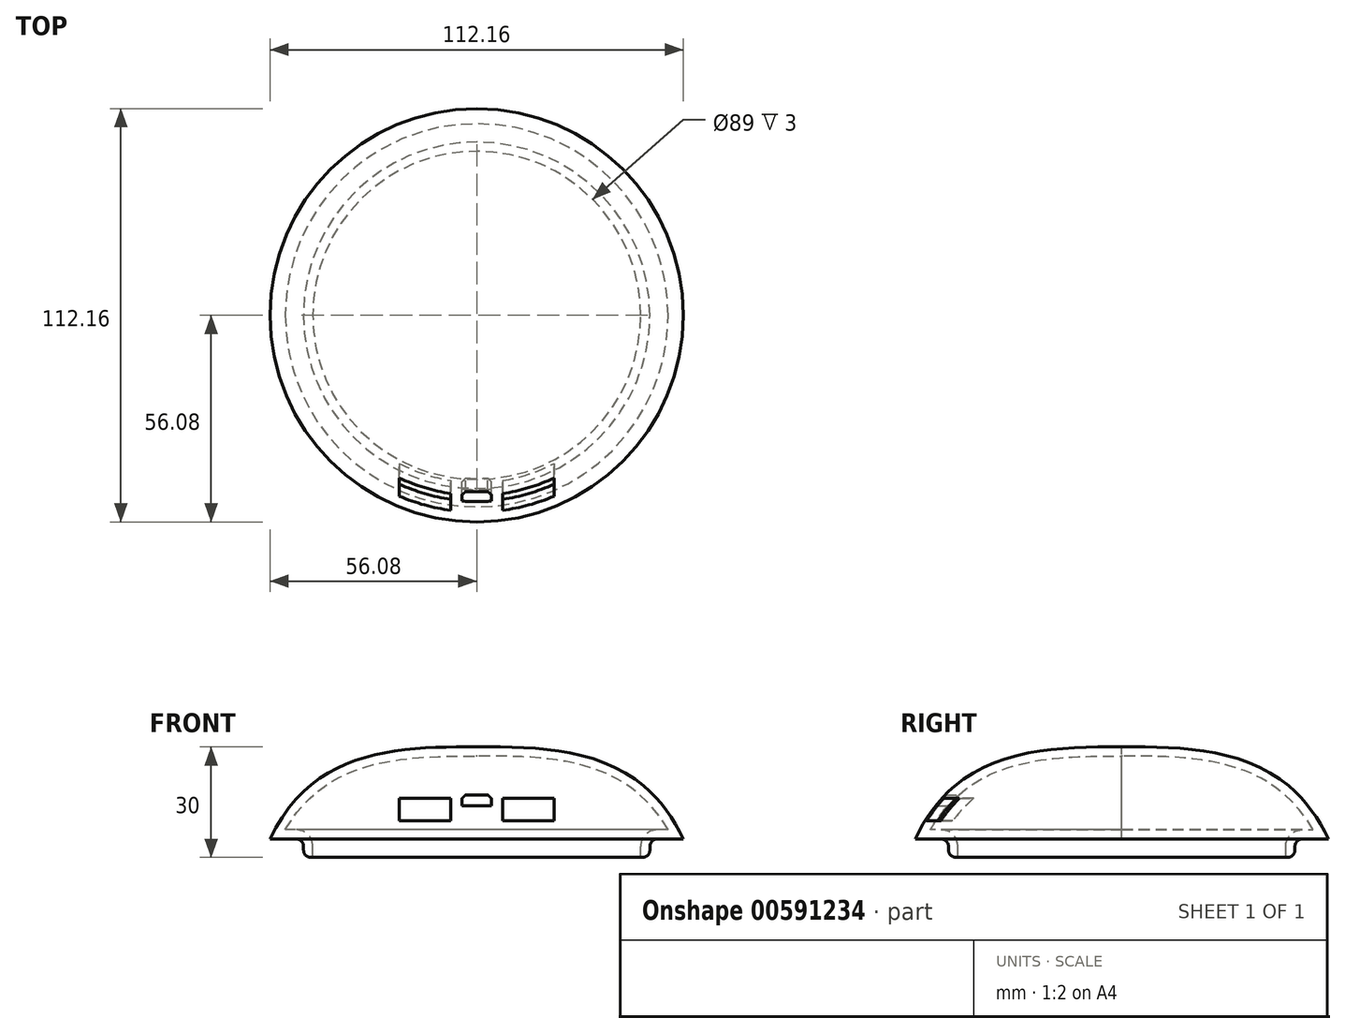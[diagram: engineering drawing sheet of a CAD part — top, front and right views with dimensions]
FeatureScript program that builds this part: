
annotation { "Feature Type Name" : "Feature", "Feature Type Description" : "" }
export const myFeature = defineFeature(function(context is Context, id is Id, definition is map)
    precondition{}
    {
        {
            var Q0;
            Q0=qCreatedBy(makeId("Front.planeOp"),FACE);
            var sketch = newSketch(context, id + "F0", { "sketchPlane" : qUnion([Q0])});
            skLineSegment(sketch, "E0", {"start": v(0, 0) * mm, "end": v(0, 35) * mm, "construction": true});
            skLineSegment(sketch, "E1", {"start": v(0, 0) * mm, "end": v(-45, 0) * mm, "construction": true});
            skFitSpline(sketch, "E2", {"points": [v(0, 35) * mm, v(-48.2, 26.6) * mm, v(-65, 0) * mm], "startDerivative": vector(-121.59, 0) * mm, "endDerivative": vector(-32.6, -91.94) * mm, "construction": true});
            skLineSegment(sketch, "E3", {"start": v(0, 0) * mm, "end": v(-45, 0) * mm});
            skLineSegment(sketch, "E4", {"start": v(-47, 2) * mm, "end": v(-47, 3) * mm});
            skLineSegment(sketch, "E5", {"start": v(-49, 5) * mm, "end": v(-63.16, 5) * mm, "construction": true});
            skPoint(sketch, "E6.newPointA", {"position": v(-47, 0) * mm});
            skArc(sketch, "E6.filletArc", {"start": v(-47, 2) * mm, "mid": v(-46.41, 0.59) * mm, "end": v(-45, 0) * mm});
            skPoint(sketch, "E7.visualSharp", {"position": v(-47, 5) * mm});
            skArc(sketch, "E7.filletArc", {"start": v(-47, 3) * mm, "mid": v(-47.59, 4.41) * mm, "end": v(-49, 5) * mm});
            skFitSpline(sketch, "E8", {"points": [v(-56.08, 5) * mm, v(0, 30) * mm], "startDerivative": vector(34.85, 74.1) * mm, "endDerivative": vector(63.57, 0) * mm});
            skLineSegment(sketch, "E9", {"start": v(-56.08, 5) * mm, "end": v(-49, 5) * mm});
            skLineSegment(sketch, "E10", {"start": v(0, 30) * mm, "end": v(0, 0) * mm});
            skSolve(sketch);
        }
        {
            var Q0;
            Q0=makeQuery(id+"F0.imprint","IMPRINT",FACE,{"disambiguationData":[TD([[makeQuery(id+"F0.imprint","IMPRINT",EDGE,{"derivedFrom":sQuery(id+"F0.wireOp",EDGE,"E3")}),-1.0]])]});
            var Q1;
            Q1=sQuery(id+"F0.wireOp",EDGE,"E10");
            revolve(context, id + "F1", {"entities" : qUnion([Q0]), "axis" : qUnion([Q1]), "revolveType" : RevolveType.FULL});
        }
        {
            var Q0;
            Q0=qCreatedBy(makeId("Top.planeOp"),FACE);
            var sketch = newSketch(context, id + "F2", { "sketchPlane" : qUnion([Q0])});
            skLineSegment(sketch, "E11.bottom", {"start": v(35, 37.5) * mm, "end": v(-35, 37.5) * mm, "construction": true});
            skLineSegment(sketch, "E11.top", {"start": v(35, -37.5) * mm, "end": v(-35, -37.5) * mm, "construction": true});
            skLineSegment(sketch, "E11.left", {"start": v(35, 37.5) * mm, "end": v(35, -37.5) * mm, "construction": true});
            skLineSegment(sketch, "E11.right", {"start": v(-35, 37.5) * mm, "end": v(-35, -37.5) * mm, "construction": true});
            skSolve(sketch);
        }
        {
            var Q0;
            Q0=qCreatedBy(makeId("Front.planeOp"),FACE);
            var sketch = newSketch(context, id + "F3", { "sketchPlane" : qUnion([Q0])});
            skLineSegment(sketch, "E12.bottom", {"start": v(-21, 16) * mm, "end": v(-7, 16) * mm});
            skLineSegment(sketch, "E12.top", {"start": v(-21, 10) * mm, "end": v(-7, 10) * mm});
            skLineSegment(sketch, "E12.left", {"start": v(-21, 16) * mm, "end": v(-21, 10) * mm});
            skLineSegment(sketch, "E12.right", {"start": v(-7, 16) * mm, "end": v(-7, 10) * mm});
            skLineSegment(sketch, "E13.MirrorCS", {"start": v(21, 16) * mm, "end": v(21, 10) * mm});
            skLineSegment(sketch, "E14.MirrorCS", {"start": v(21, 10) * mm, "end": v(7, 10) * mm});
            skLineSegment(sketch, "E15.MirrorCS", {"start": v(21, 16) * mm, "end": v(7, 16) * mm});
            skLineSegment(sketch, "E16.MirrorCS", {"start": v(7, 16) * mm, "end": v(7, 10) * mm});
            skLineSegment(sketch, "E17.bottom", {"start": v(-4, 14) * mm, "end": v(4, 14) * mm});
            skLineSegment(sketch, "E17.top", {"start": v(-4, 16) * mm, "end": v(4, 16) * mm});
            skLineSegment(sketch, "E17.left", {"start": v(-4, 14) * mm, "end": v(-4, 16) * mm});
            skLineSegment(sketch, "E17.right", {"start": v(4, 14) * mm, "end": v(4, 16) * mm});
            skLineSegment(sketch, "E18", {"start": v(-4, 16) * mm, "end": v(-3, 17) * mm});
            skLineSegment(sketch, "E19", {"start": v(-3, 17) * mm, "end": v(3, 17) * mm});
            skLineSegment(sketch, "E20", {"start": v(3, 17) * mm, "end": v(4, 16) * mm});
            skSolve(sketch);
        }
        {
            var Q0;
            Q0=makeQuery(id+"F1.opRevolve","SWEPT_FACE",FACE,{"disambiguationData":[OSD([sQuery(id+"F0.wireOp",EDGE,"E3")])]});
            shell(context, id + "F4", {"entities" : qUnion([Q0]), "thickness" : 2.5 * mm});
        }
        {
            var Q0;
            Q0 = qSketchRegion(id + "F3", true);
            extrude(context, id + "F5", {"entities" : qUnion([Q0]), "operationType" : NewBodyOperationType.REMOVE, "depth" : 70 * mm, "offsetDistance" : 25 * mm});
        }
    });
